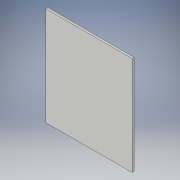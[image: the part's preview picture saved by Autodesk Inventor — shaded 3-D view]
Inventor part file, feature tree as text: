
AUTODESK INVENTOR PART (.ipt)
format: ipt  version: 2017 (Build 210142000, 142)  size: 88,576 bytes
history: native  units: in
note: dims shown in document units (in); Inventor stores cm internally (conversion verified against a paired STEP export)
features: extrude x1, sketch x1
ambient origin geometry x8: Origin, YZ Plane, XZ Plane, XY Plane, X Axis, Y Axis, Z Axis, Center Point
bodies: Solid1 (feature_tree)
feature tree (2):
  extrude  "Extrusion1"  Depth=11.425in
  sketch  "Sketch1"  dims[d0=10.0in d1=11.425in d2=0.25in d3=0.0in]
